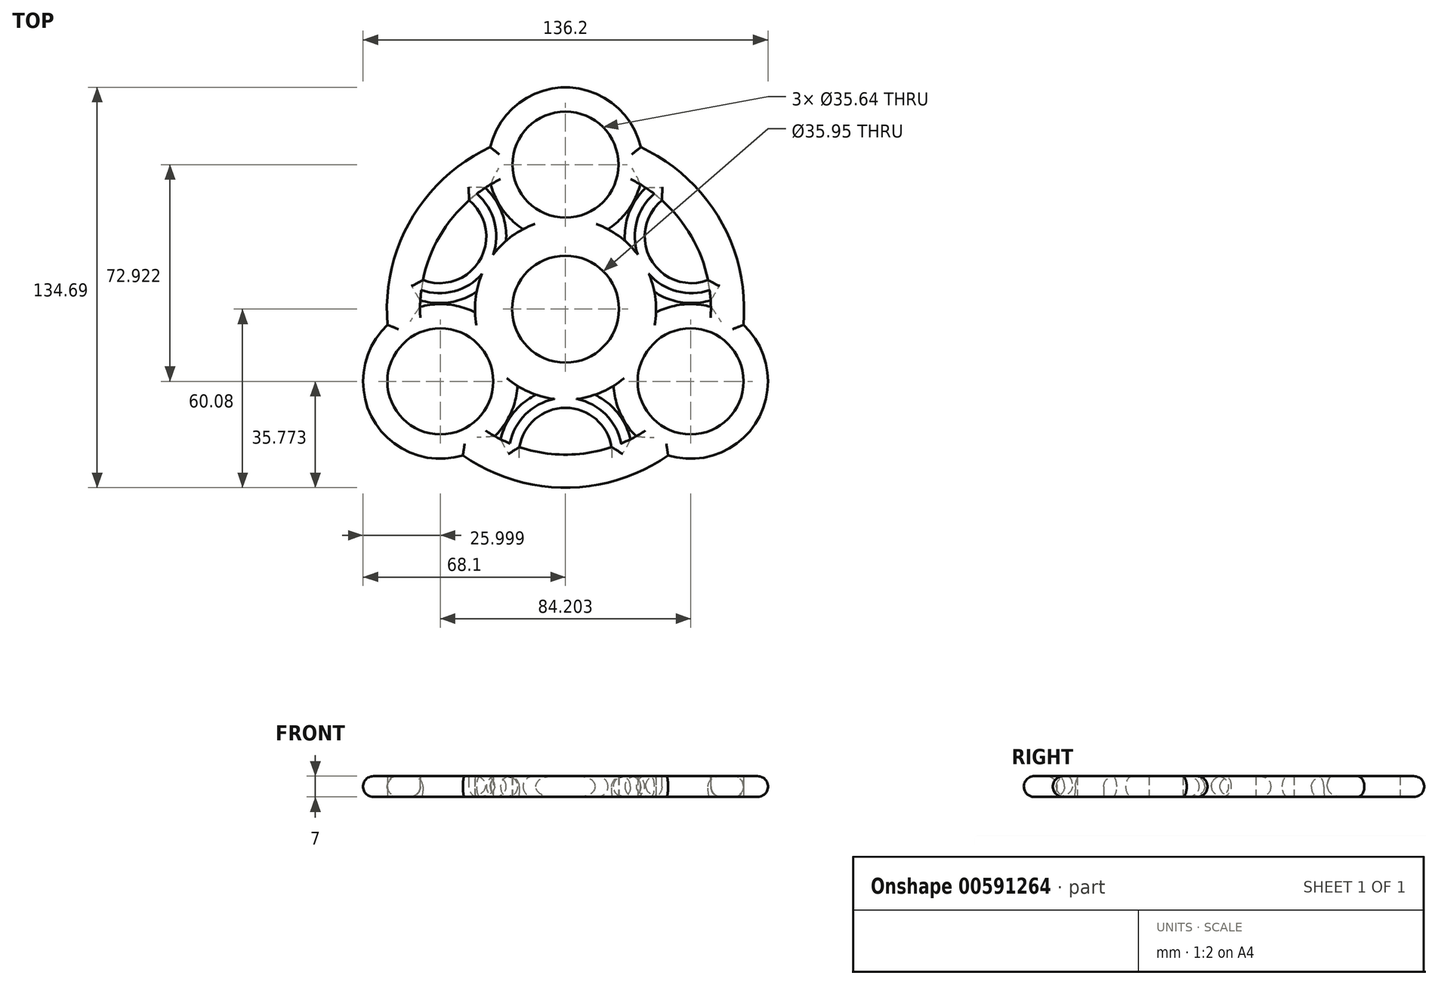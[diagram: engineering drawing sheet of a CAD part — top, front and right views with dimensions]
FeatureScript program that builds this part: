
annotation { "Feature Type Name" : "Feature", "Feature Type Description" : "" }
export const myFeature = defineFeature(function(context is Context, id is Id, definition is map)
    precondition{}
    {
        {
            var Q0;
            Q0=qCreatedBy(makeId("Top.planeOp"),FACE);
            var sketch = newSketch(context, id + "F0", { "sketchPlane" : qUnion([Q0])});
            skCircle(sketch, "E0", {"center": v(0, 0) * mm, "radius": 17.97 * mm});
            skCircle(sketch, "E1", {"center": v(0, 48.61) * mm, "radius": 17.82 * mm});
            skArc(sketch, "E2", {"start": v(14.3, 26.9) * mm, "mid": v(21.1, 33.43) * mm, "end": v(25.14, 41.97) * mm});
            skArc(sketch, "E3", {"start": v(30.44, -1.07) * mm, "mid": v(30.36, 2.38) * mm, "end": v(29.9, 5.8) * mm});
            skArc(sketch, "E4.1.0", {"start": v(-30.44, -1.07) * mm, "mid": v(-39.5, 1.56) * mm, "end": v(-48.91, 0.79) * mm});
            skCircle(sketch, "E4.1.1", {"center": v(-42.1, -24.3) * mm, "radius": 17.82 * mm});
            skArc(sketch, "E4.2.0", {"start": v(16.15, -25.82) * mm, "mid": v(18.4, -35) * mm, "end": v(23.78, -42.75) * mm});
            skCircle(sketch, "E4.2.1", {"center": v(42.1, -24.3) * mm, "radius": 17.82 * mm});
            skArc(sketch, "E5", {"start": v(-25.33, 54.48) * mm, "mid": v(-52.03, 30.04) * mm, "end": v(-59.84, -5.3) * mm});
            skArc(sketch, "E6", {"start": v(-25.14, 41.97) * mm, "mid": v(-26.07, 41.4) * mm, "end": v(-26.99, 40.8) * mm});
            skArc(sketch, "E7.trimOffspring", {"start": v(-23.78, -42.75) * mm, "mid": v(-22.81, -43.27) * mm, "end": v(-21.84, -43.77) * mm});
            skArc(sketch, "E8.trimOffspring", {"start": v(-34.51, -49.18) * mm, "mid": v(0, -60.08) * mm, "end": v(34.51, -49.18) * mm});
            skArc(sketch, "E9.trimOffspring", {"start": v(48.91, 0.79) * mm, "mid": v(48.88, 1.88) * mm, "end": v(48.83, 2.97) * mm});
            skArc(sketch, "E10.trimOffspring", {"start": v(59.84, -5.3) * mm, "mid": v(52.03, 30.04) * mm, "end": v(25.33, 54.48) * mm});
            skArc(sketch, "E11.trimOffspring", {"start": v(-16.15, -25.82) * mm, "mid": v(0, -30.45) * mm, "end": v(16.15, -25.82) * mm});
            skArc(sketch, "E12.trimOffspring", {"start": v(-14.3, 26.9) * mm, "mid": v(-17.24, 25.1) * mm, "end": v(-19.97, 22.99) * mm});
            skArc(sketch, "E13", {"start": v(29.9, 5.8) * mm, "mid": v(39.04, 2.27) * mm, "end": v(48.83, 2.97) * mm});
            skArc(sketch, "E14", {"start": v(32.43, 36.63) * mm, "mid": v(28.76, 16.6) * mm, "end": v(47.93, 9.77) * mm});
            skArc(sketch, "E15.trimOffspring", {"start": v(19.97, 22.99) * mm, "mid": v(17.24, 25.1) * mm, "end": v(14.3, 26.9) * mm});
            skArc(sketch, "E16.trimOffspring", {"start": v(26.99, 40.8) * mm, "mid": v(21.49, 32.68) * mm, "end": v(19.97, 22.99) * mm});
            skArc(sketch, "E17.1.0", {"start": v(-47.93, 9.77) * mm, "mid": v(-28.76, 16.6) * mm, "end": v(-32.43, 36.63) * mm});
            skArc(sketch, "E17.1.1", {"start": v(-19.97, 22.99) * mm, "mid": v(-21.49, 32.68) * mm, "end": v(-26.99, 40.8) * mm});
            skArc(sketch, "E17.1.2", {"start": v(-48.83, 2.97) * mm, "mid": v(-39.04, 2.27) * mm, "end": v(-29.9, 5.8) * mm});
            skArc(sketch, "E17.2.0", {"start": v(15.5, -46.4) * mm, "mid": v(0, -33.2) * mm, "end": v(-15.5, -46.4) * mm});
            skArc(sketch, "E17.2.1", {"start": v(-9.92, -28.8) * mm, "mid": v(-17.56, -34.95) * mm, "end": v(-21.84, -43.77) * mm});
            skArc(sketch, "E17.2.2", {"start": v(21.84, -43.77) * mm, "mid": v(17.56, -34.95) * mm, "end": v(9.92, -28.8) * mm});
            skArc(sketch, "E18.trimOffspring", {"start": v(-29.9, 5.8) * mm, "mid": v(-30.36, 2.38) * mm, "end": v(-30.44, -1.07) * mm});
            skArc(sketch, "E19.trimOffspring", {"start": v(-48.83, 2.97) * mm, "mid": v(-48.88, 1.88) * mm, "end": v(-48.91, 0.79) * mm});
            skArc(sketch, "E20.trimOffspring", {"start": v(-32.43, 36.63) * mm, "mid": v(-42.36, 24.46) * mm, "end": v(-47.93, 9.77) * mm});
            skArc(sketch, "E21.trimOffspring", {"start": v(26.99, 40.8) * mm, "mid": v(26.07, 41.4) * mm, "end": v(25.14, 41.97) * mm});
            skArc(sketch, "E22.trimOffspring", {"start": v(47.93, 9.77) * mm, "mid": v(42.36, 24.46) * mm, "end": v(32.43, 36.63) * mm});
            skArc(sketch, "E23.trimOffspring", {"start": v(-15.5, -46.4) * mm, "mid": v(0, -48.92) * mm, "end": v(15.5, -46.4) * mm});
            skArc(sketch, "E24.trimOffspring", {"start": v(21.84, -43.77) * mm, "mid": v(22.81, -43.27) * mm, "end": v(23.78, -42.75) * mm});
            skArc(sketch, "E25.trimOffspring", {"start": v(34.51, -49.18) * mm, "mid": v(64.62, -37.3) * mm, "end": v(59.84, -5.3) * mm});
            skArc(sketch, "E26.trimOffspring", {"start": v(-23.78, -42.75) * mm, "mid": v(-18.4, -35) * mm, "end": v(-16.15, -25.82) * mm});
            skArc(sketch, "E27.trimOffspring", {"start": v(-59.84, -5.3) * mm, "mid": v(-64.62, -37.3) * mm, "end": v(-34.51, -49.18) * mm});
            skArc(sketch, "E28.trimOffspring", {"start": v(-25.14, 41.97) * mm, "mid": v(-21.1, 33.43) * mm, "end": v(-14.3, 26.9) * mm});
            skArc(sketch, "E29.trimOffspring", {"start": v(25.33, 54.48) * mm, "mid": v(0, 74.61) * mm, "end": v(-25.33, 54.48) * mm});
            skArc(sketch, "E30.trimOffspring", {"start": v(48.91, 0.79) * mm, "mid": v(39.5, 1.56) * mm, "end": v(30.44, -1.07) * mm});
            skSolve(sketch);
        }
        {
            var Q0;
            Q0=makeQuery(id+"F0.imprint","IMPRINT",FACE,{"disambiguationData":[TD([[makeQuery(id+"F0.imprint","IMPRINT",EDGE,{"derivedFrom":sQuery(id+"F0.wireOp",EDGE,"E0")}),-1.0]])]});
            extrude(context, id + "F1", {"entities" : qUnion([Q0]), "depth" : 7 * mm, "offsetDistance" : 25 * mm});
        }
        {
            var Q0;
            Q0=makeQuery(id+"F1.opExtrude","CAP_EDGE",EDGE,{"disambiguationData":[OSD([sQuery(id+"F0.wireOp",EDGE,"E27.trimOffspring")])],"isStart":false});
            var Q1;
            Q1=makeQuery(id+"F1.opExtrude","CAP_EDGE",EDGE,{"disambiguationData":[OSD([sQuery(id+"F0.wireOp",EDGE,"E5")])],"isStart":false});
            var Q2;
            Q2=makeQuery(id+"F1.opExtrude","CAP_EDGE",EDGE,{"disambiguationData":[OSD([sQuery(id+"F0.wireOp",EDGE,"E8.trimOffspring")])],"isStart":false});
            var Q3;
            Q3=makeQuery(id+"F1.opExtrude","CAP_EDGE",EDGE,{"disambiguationData":[OSD([sQuery(id+"F0.wireOp",EDGE,"E25.trimOffspring")])],"isStart":false});
            var Q4;
            Q4=makeQuery(id+"F1.opExtrude","CAP_EDGE",EDGE,{"disambiguationData":[OSD([sQuery(id+"F0.wireOp",EDGE,"E10.trimOffspring")])],"isStart":false});
            var Q5;
            Q5=makeQuery(id+"F1.opExtrude","CAP_EDGE",EDGE,{"disambiguationData":[OSD([sQuery(id+"F0.wireOp",EDGE,"E29.trimOffspring")])],"isStart":false});
            fillet(context, id + "F2", {"entities" : qUnion([Q0, Q1, Q2, Q3, Q4, Q5]), "radius" : 3.5 * mm, "tangentPropagation" : true, "allowEdgeOverflow" : false});
        }
        {
            var Q0;
            Q0=makeQuery(id+"F1.opExtrude","CAP_EDGE",EDGE,{"disambiguationData":[OSD([sQuery(id+"F0.wireOp",EDGE,"E5")])],"isStart":true});
            var Q1;
            Q1=makeQuery(id+"F1.opExtrude","CAP_EDGE",EDGE,{"disambiguationData":[OSD([sQuery(id+"F0.wireOp",EDGE,"E29.trimOffspring")])],"isStart":true});
            var Q2;
            Q2=makeQuery(id+"F1.opExtrude","CAP_EDGE",EDGE,{"disambiguationData":[OSD([sQuery(id+"F0.wireOp",EDGE,"E10.trimOffspring")])],"isStart":true});
            var Q3;
            Q3=makeQuery(id+"F1.opExtrude","CAP_EDGE",EDGE,{"disambiguationData":[OSD([sQuery(id+"F0.wireOp",EDGE,"E25.trimOffspring")])],"isStart":true});
            var Q4;
            Q4=makeQuery(id+"F1.opExtrude","CAP_EDGE",EDGE,{"disambiguationData":[OSD([sQuery(id+"F0.wireOp",EDGE,"E27.trimOffspring")])],"isStart":true});
            var Q5;
            Q5=makeQuery(id+"F1.opExtrude","CAP_EDGE",EDGE,{"disambiguationData":[OSD([sQuery(id+"F0.wireOp",EDGE,"E8.trimOffspring")])],"isStart":true});
            fillet(context, id + "F3", {"entities" : qUnion([Q0, Q1, Q2, Q3, Q4, Q5]), "radius" : 3.5 * mm, "tangentPropagation" : true, "allowEdgeOverflow" : false});
        }
        {
            var Q0;
            Q0=makeQuery(id+"F1.opExtrude","CAP_EDGE",EDGE,{"disambiguationData":[OSD([sQuery(id+"F0.wireOp",EDGE,"E20.trimOffspring")])],"isStart":false});
            var Q1;
            Q1=makeQuery(id+"F1.opExtrude","CAP_EDGE",EDGE,{"disambiguationData":[OSD([sQuery(id+"F0.wireOp",EDGE,"E17.1.0")])],"isStart":false});
            var Q2;
            Q2=makeQuery(id+"F1.opExtrude","CAP_EDGE",EDGE,{"disambiguationData":[OSD([sQuery(id+"F0.wireOp",EDGE,"E14")])],"isStart":false});
            var Q3;
            Q3=makeQuery(id+"F1.opExtrude","CAP_EDGE",EDGE,{"disambiguationData":[OSD([sQuery(id+"F0.wireOp",EDGE,"E22.trimOffspring")])],"isStart":false});
            var Q4;
            Q4=makeQuery(id+"F1.opExtrude","CAP_EDGE",EDGE,{"disambiguationData":[OSD([sQuery(id+"F0.wireOp",EDGE,"E23.trimOffspring")])],"isStart":false});
            var Q5;
            Q5=makeQuery(id+"F1.opExtrude","CAP_EDGE",EDGE,{"disambiguationData":[OSD([sQuery(id+"F0.wireOp",EDGE,"E17.2.0")])],"isStart":false});
            fillet(context, id + "F4", {"entities" : qUnion([Q0, Q1, Q2, Q3, Q4, Q5]), "radius" : 3.5 * mm, "tangentPropagation" : true, "allowEdgeOverflow" : false});
        }
        {
            var Q0;
            {var subQ0=sQuery(id+"F0.wireOp",EDGE,"E22.trimOffspring");Q0=makeQuery(id+"F4.opFillet","BLEND_EDGE",EDGE,{"blendedFrom":[makeQuery(id+"F1.opExtrude","CAP_EDGE",EDGE,{"disambiguationData":[OSD([subQ0])],"isStart":false}),makeQuery(id+"F1.opExtrude","SWEPT_FACE",FACE,{"disambiguationData":[OSD([subQ0])]})],"blendedInto":[makeQuery(id+"F1.opExtrude","SWEPT_FACE",FACE,{"disambiguationData":[OSD([subQ0])]})]});}
            var Q1;
            Q1=makeQuery(id+"F1.opExtrude","CAP_EDGE",EDGE,{"disambiguationData":[OSD([sQuery(id+"F0.wireOp",EDGE,"E14")])],"isStart":true});
            var Q2;
            {var subQ0=sQuery(id+"F0.wireOp",EDGE,"E20.trimOffspring");Q2=makeQuery(id+"F4.opFillet","BLEND_EDGE",EDGE,{"blendedFrom":[makeQuery(id+"F1.opExtrude","CAP_EDGE",EDGE,{"disambiguationData":[OSD([subQ0])],"isStart":false}),makeQuery(id+"F1.opExtrude","SWEPT_FACE",FACE,{"disambiguationData":[OSD([subQ0])]})],"blendedInto":[makeQuery(id+"F1.opExtrude","SWEPT_FACE",FACE,{"disambiguationData":[OSD([subQ0])]})]});}
            var Q3;
            Q3=makeQuery(id+"F1.opExtrude","CAP_EDGE",EDGE,{"disambiguationData":[OSD([sQuery(id+"F0.wireOp",EDGE,"E17.1.0")])],"isStart":true});
            var Q4;
            {var subQ0=sQuery(id+"F0.wireOp",EDGE,"E17.2.0");Q4=makeQuery(id+"F4.opFillet","BLEND_EDGE",EDGE,{"blendedFrom":[makeQuery(id+"F1.opExtrude","CAP_EDGE",EDGE,{"disambiguationData":[OSD([subQ0])],"isStart":false}),makeQuery(id+"F1.opExtrude","SWEPT_FACE",FACE,{"disambiguationData":[OSD([subQ0])]})],"blendedInto":[makeQuery(id+"F1.opExtrude","SWEPT_FACE",FACE,{"disambiguationData":[OSD([subQ0])]})]});}
            var Q5;
            Q5=makeQuery(id+"F1.opExtrude","CAP_EDGE",EDGE,{"disambiguationData":[OSD([sQuery(id+"F0.wireOp",EDGE,"E23.trimOffspring")])],"isStart":true});
            fillet(context, id + "F5", {"entities" : qUnion([Q0, Q1, Q2, Q3, Q4, Q5]), "radius" : 3.5 * mm, "tangentPropagation" : true, "allowEdgeOverflow" : false});
        }
        {
            var Q0;
            Q0=makeQuery(id+"F1.opExtrude","CAP_EDGE",EDGE,{"disambiguationData":[OSD([sQuery(id+"F0.wireOp",EDGE,"E9.trimOffspring")])],"isStart":true});
            var Q1;
            Q1=makeQuery(id+"F1.opExtrude","CAP_EDGE",EDGE,{"disambiguationData":[OSD([sQuery(id+"F0.wireOp",EDGE,"E13")])],"isStart":true});
            var Q2;
            Q2=makeQuery(id+"F1.opExtrude","CAP_EDGE",EDGE,{"disambiguationData":[OSD([sQuery(id+"F0.wireOp",EDGE,"E30.trimOffspring")])],"isStart":true});
            var Q3;
            Q3=makeQuery(id+"F1.opExtrude","CAP_EDGE",EDGE,{"disambiguationData":[OSD([sQuery(id+"F0.wireOp",EDGE,"E17.2.2")])],"isStart":true});
            var Q4;
            Q4=makeQuery(id+"F1.opExtrude","CAP_EDGE",EDGE,{"disambiguationData":[OSD([sQuery(id+"F0.wireOp",EDGE,"E24.trimOffspring")])],"isStart":true});
            var Q5;
            Q5=makeQuery(id+"F1.opExtrude","CAP_EDGE",EDGE,{"disambiguationData":[OSD([sQuery(id+"F0.wireOp",EDGE,"E4.2.0")])],"isStart":true});
            var Q6;
            Q6=makeQuery(id+"F1.opExtrude","CAP_EDGE",EDGE,{"disambiguationData":[OSD([sQuery(id+"F0.wireOp",EDGE,"E26.trimOffspring")])],"isStart":true});
            var Q7;
            Q7=makeQuery(id+"F1.opExtrude","CAP_EDGE",EDGE,{"disambiguationData":[OSD([sQuery(id+"F0.wireOp",EDGE,"E17.2.1")])],"isStart":true});
            var Q8;
            Q8=makeQuery(id+"F1.opExtrude","CAP_EDGE",EDGE,{"disambiguationData":[OSD([sQuery(id+"F0.wireOp",EDGE,"E7.trimOffspring")])],"isStart":true});
            var Q9;
            Q9=makeQuery(id+"F1.opExtrude","CAP_EDGE",EDGE,{"disambiguationData":[OSD([sQuery(id+"F0.wireOp",EDGE,"E4.1.0")])],"isStart":true});
            var Q10;
            Q10=makeQuery(id+"F1.opExtrude","CAP_EDGE",EDGE,{"disambiguationData":[OSD([sQuery(id+"F0.wireOp",EDGE,"E19.trimOffspring")])],"isStart":true});
            var Q11;
            Q11=makeQuery(id+"F1.opExtrude","CAP_EDGE",EDGE,{"disambiguationData":[OSD([sQuery(id+"F0.wireOp",EDGE,"E17.1.2")])],"isStart":true});
            var Q12;
            Q12=makeQuery(id+"F1.opExtrude","CAP_EDGE",EDGE,{"disambiguationData":[OSD([sQuery(id+"F0.wireOp",EDGE,"E6")])],"isStart":true});
            var Q13;
            Q13=makeQuery(id+"F1.opExtrude","CAP_EDGE",EDGE,{"disambiguationData":[OSD([sQuery(id+"F0.wireOp",EDGE,"E17.1.1")])],"isStart":true});
            var Q14;
            Q14=makeQuery(id+"F1.opExtrude","CAP_EDGE",EDGE,{"disambiguationData":[OSD([sQuery(id+"F0.wireOp",EDGE,"E28.trimOffspring")])],"isStart":true});
            var Q15;
            Q15=makeQuery(id+"F1.opExtrude","CAP_EDGE",EDGE,{"disambiguationData":[OSD([sQuery(id+"F0.wireOp",EDGE,"E21.trimOffspring")])],"isStart":true});
            var Q16;
            Q16=makeQuery(id+"F1.opExtrude","CAP_EDGE",EDGE,{"disambiguationData":[OSD([sQuery(id+"F0.wireOp",EDGE,"E2")])],"isStart":true});
            var Q17;
            Q17=makeQuery(id+"F1.opExtrude","CAP_EDGE",EDGE,{"disambiguationData":[OSD([sQuery(id+"F0.wireOp",EDGE,"E16.trimOffspring")])],"isStart":true});
            fillet(context, id + "F6", {"entities" : qUnion([Q0, Q1, Q2, Q3, Q4, Q5, Q6, Q7, Q8, Q9, Q10, Q11, Q12, Q13, Q14, Q15, Q16, Q17]), "radius" : 3.5 * mm, "tangentPropagation" : true, "allowEdgeOverflow" : false});
        }
        {
            var Q0;
            Q0=makeQuery(id+"F1.opExtrude","CAP_EDGE",EDGE,{"disambiguationData":[OSD([sQuery(id+"F0.wireOp",EDGE,"E2")])],"isStart":false});
            var Q1;
            Q1=makeQuery(id+"F1.opExtrude","CAP_EDGE",EDGE,{"disambiguationData":[OSD([sQuery(id+"F0.wireOp",EDGE,"E16.trimOffspring")])],"isStart":false});
            var Q2;
            Q2=makeQuery(id+"F1.opExtrude","CAP_EDGE",EDGE,{"disambiguationData":[OSD([sQuery(id+"F0.wireOp",EDGE,"E30.trimOffspring")])],"isStart":false});
            var Q3;
            Q3=makeQuery(id+"F1.opExtrude","CAP_EDGE",EDGE,{"disambiguationData":[OSD([sQuery(id+"F0.wireOp",EDGE,"E13")])],"isStart":false});
            var Q4;
            Q4=makeQuery(id+"F1.opExtrude","CAP_EDGE",EDGE,{"disambiguationData":[OSD([sQuery(id+"F0.wireOp",EDGE,"E4.2.0")])],"isStart":false});
            var Q5;
            Q5=makeQuery(id+"F1.opExtrude","CAP_EDGE",EDGE,{"disambiguationData":[OSD([sQuery(id+"F0.wireOp",EDGE,"E17.2.2")])],"isStart":false});
            var Q6;
            Q6=makeQuery(id+"F1.opExtrude","CAP_EDGE",EDGE,{"disambiguationData":[OSD([sQuery(id+"F0.wireOp",EDGE,"E17.2.1")])],"isStart":false});
            var Q7;
            Q7=makeQuery(id+"F1.opExtrude","CAP_EDGE",EDGE,{"disambiguationData":[OSD([sQuery(id+"F0.wireOp",EDGE,"E26.trimOffspring")])],"isStart":false});
            var Q8;
            Q8=makeQuery(id+"F1.opExtrude","CAP_EDGE",EDGE,{"disambiguationData":[OSD([sQuery(id+"F0.wireOp",EDGE,"E4.1.0")])],"isStart":false});
            var Q9;
            Q9=makeQuery(id+"F1.opExtrude","CAP_EDGE",EDGE,{"disambiguationData":[OSD([sQuery(id+"F0.wireOp",EDGE,"E17.1.2")])],"isStart":false});
            var Q10;
            Q10=makeQuery(id+"F1.opExtrude","CAP_EDGE",EDGE,{"disambiguationData":[OSD([sQuery(id+"F0.wireOp",EDGE,"E17.1.1")])],"isStart":false});
            var Q11;
            Q11=makeQuery(id+"F1.opExtrude","CAP_EDGE",EDGE,{"disambiguationData":[OSD([sQuery(id+"F0.wireOp",EDGE,"E28.trimOffspring")])],"isStart":false});
            fillet(context, id + "F7", {"entities" : qUnion([Q0, Q1, Q2, Q3, Q4, Q5, Q6, Q7, Q8, Q9, Q10, Q11]), "radius" : 3.5 * mm, "tangentPropagation" : true, "allowEdgeOverflow" : false});
        }
    });
